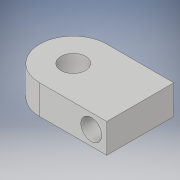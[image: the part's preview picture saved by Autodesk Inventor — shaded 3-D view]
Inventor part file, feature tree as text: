
AUTODESK INVENTOR PART (.ipt)
format: ipt  version: 2018 (Build 220112000, 112)  size: 135,168 bytes
history: native  units: in
note: dims shown in document units (in); Inventor stores cm internally (conversion verified against a paired STEP export)
features: sketch x7, extrude x6
ambient origin geometry x8: Origin, YZ Plane, XZ Plane, XY Plane, X Axis, Y Axis, Z Axis, Center Point
bodies: Solid1 (feature_tree)
feature tree (13):
  extrude  "Extrusion1"  Depth=0.8661in
  sketch  "Sketch2"  dims[d2=0.315in d3=0.4331in]
  sketch  "Sketch3"  dims[d4=0.378in d5=0.0in d6=0.2in]
  extrude  "Extrusion2"  Depth=0.4331in
  extrude  "Extrusion3"  Depth=0.378in
  extrude  "Extrusion4"  Depth=0.8661in
  extrude  "Extrusion5"  Depth=0.378in TaperAngle=0.0deg
  extrude  "Extrusion6"  Depth=0.378in
  sketch  "Sketch1"  dims[d0=0.6299in d1=0.8661in]
  sketch  "Sketch4"  dims[d8=0.2697in d10=0.8661in]
  sketch  "Sketch5"  dims[d11=0.378in d12=0.0in d13=0.378in d14=0.0in]
  sketch  "Sketch6"  dims[d15=0.378in d16=0.0in d17=0.5in]
  sketch  "Sketch7"  dims[d18=0.5in d19=0.0in d20=0.3189in d21=0.3937in d22=0.0in]
